# Revit family: Shower-Rainhead-KOHLER-Open_Rain-K-26301IN_1
name_source: partatom
category: Plumbing Fixtures
revit_build: Autodesk Revit 2017 (Build: 20160225_1515(x64)
units: mm (PartAtom-declared; Revit-internal decimal feet)

## family parameters
Cut with Voids When Loaded = No
Host = Face
OmniClass Number = 23.31.17.00
OmniClass Title = Showers
Part Type = Normal
Room Calculation Point = No
Round Connector Dimension = Use Diameter
Shared = No

## types (6) — shared parameters
ADA Compliant = No
Assembly Code = D2010700
CW Connection = No
Cold Water Inlet = Cold Water Inlet
Date Modified = 03/09/2021
Default Elevation = 42"
Description = OPEN RAIN RAINHEAD, 2.5GPM
Drain Included = No
Flow Rate = 3 GPM
HW Connection = Yes
Height = 8 7/8"
Hot Water Inlet = Hot Water Inlet
Length = 5 1/4"
Manufacturer = KOHLER Co.
Master Format 2014 = 22 42 23
Master Format 2014 Name = Residential Showers
Material = Premium Metal Construction
Panel Thickness = 13/16"
Pressure = 80.00 psi
Product Name = Open Rain
Tempered Water Inlet = Tempered Water Inlet
URL = https://www.kohler.co.in
Vent Connection = No
Waste Connection = No
Waste Water Outlet = Waste Water Outlet
WaterSense Certified = No
Width = 8 7/8"

## per-type parameters (varying)
| type | Finish | Model | Type |
| 2.5 GPM, CP-Polished Chrome | Kohler-Metal-CP-Polished_Chrome | K-26301IN-CP | 5 |
| 2.5 GPM, BN-Vibrant Brushed Nickel | Kohler-Metal-BN-Vibrant_Brushed_Nickel | K-26301IN-BN | 3 |
| 2.5 GPM, BL-Matte Black | Kohler-Metal-BL-Matte_Black | K-26301IN-BL | 2 |
| 2.5 GPM, BV-Brushed Bronze | Kohler-Metal-BV-Brushed_Bronze | K-26301IN-BV | 4 |
| 2.5 GPM, AF-Vibrant French Gold | Kohler-Metal-AF-Vibrant_French_Gold | K-26301IN-AF | 1 |
| 2.5 GPM, RGD-Polished Rose Gold | Kohler-Metal-RGD-Polished_Rose_Gold | K-26301IN-RGD | 6 |

## geometry (parser evidence)
native form markers: Sweep x5
no freeform markers — native parametric forms only
